FCSTD DOCUMENT  (FreeCAD 0.20R29603 (Git))
Label: two_wires_coax
License: All rights reserved
LicenseURL: http://en.wikipedia.org/wiki/All_rights_reserved
objects: Part::Part2DObjectPython×3
note: 3 computed .brp shape members not serialized (recipe doc carries the construction recipe); baked Part::Feature solids carry a one-line shape summary decoded from their .brp

FEATURE [Part::Part2DObjectPython] Circle  label="Conductor_0"  # Draft 2D object (typed FeaturePython)
  Area = 7853.98
  FirstAngle = 0
  LastAngle = 0
  MakeFace = true
  Radius = 50
FEATURE [Part::Part2DObjectPython] Circle001  label="Conductor_1"  # Draft 2D object (typed FeaturePython)
  Area = 12.5664
  FirstAngle = 0
  LastAngle = 0
  MakeFace = true
  Placement = pos=(-25,0,0) rot=(0,0,1;0rad)
  Radius = 2
FEATURE [Part::Part2DObjectPython] Circle002  label="Conductor_2"  # Draft 2D object (typed FeaturePython)
  Area = 12.5664
  FirstAngle = 0
  LastAngle = 0
  MakeFace = true
  Placement = pos=(25,0,0) rot=(0,0,1;0rad)
  Radius = 2
